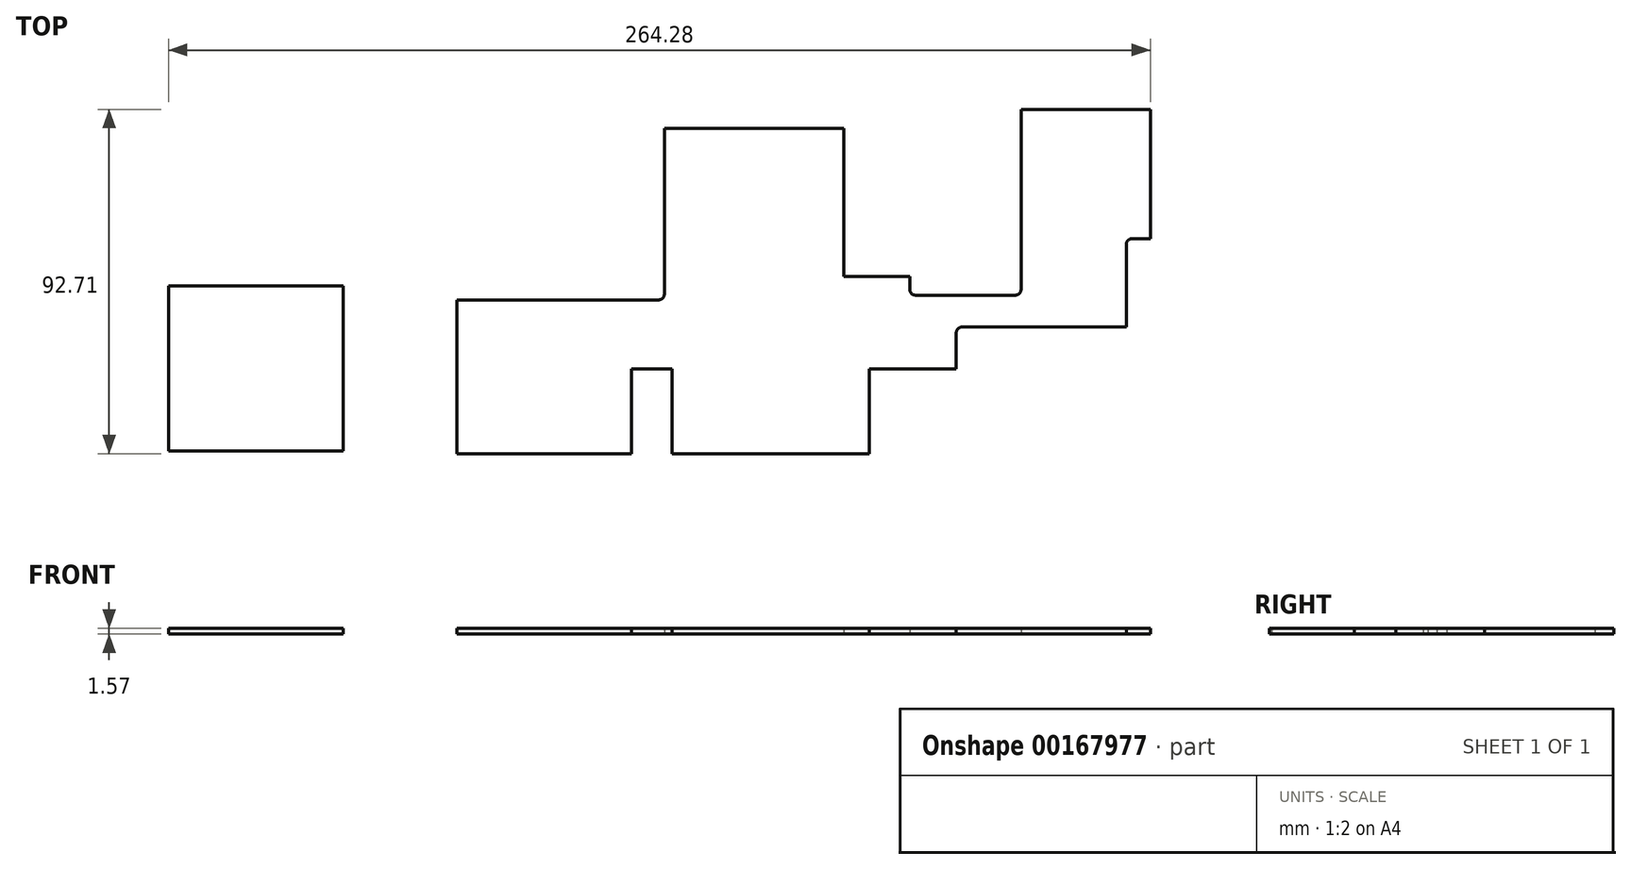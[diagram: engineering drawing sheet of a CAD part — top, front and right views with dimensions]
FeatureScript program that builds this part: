
annotation { "Feature Type Name" : "Feature", "Feature Type Description" : "" }
export const myFeature = defineFeature(function(context is Context, id is Id, definition is map)
    precondition{}
    {
        {
            var Q0;
            Q0=qCreatedBy(makeId("Top.planeOp"),FACE);
            var sketch = newSketch(context, id + "F0", { "sketchPlane" : qUnion([Q0])});
            skLineSegment(sketch, "E0.bottom", {"start": v(1.27, -0.7) * mm, "end": v(48.26, -0.7) * mm});
            skLineSegment(sketch, "E0.top", {"start": v(1.27, 40.7) * mm, "end": v(55.56, 40.7) * mm});
            skLineSegment(sketch, "E0.right", {"start": v(187.96, -0.7) * mm, "end": v(187.96, 22.66) * mm});
            skLineSegment(sketch, "E1.top", {"start": v(105.4, 86.92) * mm, "end": v(57.23, 86.92) * mm});
            skLineSegment(sketch, "E1.left", {"start": v(105.4, 53.4) * mm, "end": v(105.4, 86.92) * mm});
            skLineSegment(sketch, "E2.bottom", {"start": v(57.15, 45.77) * mm, "end": v(66.23, 45.77) * mm, "construction": true});
            skLineSegment(sketch, "E3", {"start": v(67.82, 47.36) * mm, "end": v(67.82, 86.92) * mm, "construction": true});
            skLineSegment(sketch, "E4", {"start": v(124.78, 41.96) * mm, "end": v(151.57, 41.96) * mm});
            skLineSegment(sketch, "E5.bottom", {"start": v(187.96, -0.7) * mm, "end": v(173.99, -0.7) * mm});
            skLineSegment(sketch, "E5.top", {"start": v(187.96, 92) * mm, "end": v(153.16, 92) * mm});
            skLineSegment(sketch, "E5.left", {"start": v(187.96, -0.7) * mm, "end": v(187.96, 22.66) * mm, "construction": true});
            skLineSegment(sketch, "E6.bottom", {"start": v(187.96, -0.7) * mm, "end": v(153.16, -0.7) * mm});
            skLineSegment(sketch, "E6.top", {"start": v(172.4, 74.22) * mm, "end": v(153.16, 74.22) * mm});
            skLineSegment(sketch, "E6.right", {"start": v(153.16, 43.55) * mm, "end": v(153.16, 74.22) * mm});
            skLineSegment(sketch, "E7.trimOffspring", {"start": v(173.99, 75.8) * mm, "end": v(173.99, 92) * mm});
            skLineSegment(sketch, "E8.bottom", {"start": v(187.96, 22.66) * mm, "end": v(183.07, 22.66) * mm});
            skLineSegment(sketch, "E8.top", {"start": v(187.96, 57.2) * mm, "end": v(183.07, 57.2) * mm});
            skLineSegment(sketch, "E8.right", {"start": v(181.48, 24.25) * mm, "end": v(181.48, 55.62) * mm});
            skLineSegment(sketch, "E9.trimOffspring", {"start": v(187.96, 57.2) * mm, "end": v(187.96, 92) * mm});
            skLineSegment(sketch, "E10.trimOffspring", {"start": v(187.96, 57.2) * mm, "end": v(187.96, 74.22) * mm});
            skLineSegment(sketch, "E11.bottom", {"start": v(105.4, 47.04) * mm, "end": v(123.2, 47.04) * mm});
            skLineSegment(sketch, "E11.top", {"start": v(123.2, -0.7) * mm, "end": v(123.19, -0.7) * mm});
            skLineSegment(sketch, "E11.right", {"start": v(123.2, 47.04) * mm, "end": v(123.2, 43.55) * mm});
            skLineSegment(sketch, "E12.bottom", {"start": v(105.4, 47.04) * mm, "end": v(87.19, 47.04) * mm});
            skLineSegment(sketch, "E12.top", {"start": v(105.4, 53.4) * mm, "end": v(87.19, 53.4) * mm});
            skLineSegment(sketch, "E12.right", {"start": v(85.6, 48.63) * mm, "end": v(85.6, 51.8) * mm});
            skPoint(sketch, "E13.visualSharp", {"position": v(57.15, 40.7) * mm});
            skArc(sketch, "E13.filletArc", {"start": v(55.56, 40.7) * mm, "mid": v(56.69, 41.16) * mm, "end": v(57.15, 42.28) * mm});
            skPoint(sketch, "E14.visualSharp", {"position": v(67.82, 45.77) * mm});
            skArc(sketch, "E14.filletArc", {"start": v(66.23, 45.77) * mm, "mid": v(67.35, 46.24) * mm, "end": v(67.82, 47.36) * mm});
            skPoint(sketch, "E15.visualSharp", {"position": v(85.6, 53.4) * mm});
            skArc(sketch, "E15.filletArc", {"start": v(87.19, 53.4) * mm, "mid": v(86.06, 52.93) * mm, "end": v(85.6, 51.8) * mm});
            skPoint(sketch, "E16.visualSharp", {"position": v(85.6, 47.04) * mm});
            skArc(sketch, "E16.filletArc", {"start": v(85.6, 48.63) * mm, "mid": v(86.06, 47.5) * mm, "end": v(87.19, 47.04) * mm});
            skArc(sketch, "E17.filletArc", {"start": v(123.2, 43.55) * mm, "mid": v(123.65, 42.43) * mm, "end": v(124.78, 41.96) * mm});
            skPoint(sketch, "E18.visualSharp", {"position": v(153.16, 41.96) * mm});
            skArc(sketch, "E18.filletArc", {"start": v(151.57, 41.96) * mm, "mid": v(152.7, 42.43) * mm, "end": v(153.16, 43.55) * mm});
            skPoint(sketch, "E19.visualSharp", {"position": v(173.99, 74.22) * mm});
            skArc(sketch, "E19.filletArc", {"start": v(172.4, 74.22) * mm, "mid": v(173.53, 74.69) * mm, "end": v(173.99, 75.8) * mm});
            skPoint(sketch, "E20.visualSharp", {"position": v(181.48, 57.2) * mm});
            skArc(sketch, "E20.filletArc", {"start": v(183.07, 57.2) * mm, "mid": v(181.95, 56.74) * mm, "end": v(181.48, 55.62) * mm});
            skPoint(sketch, "E21.visualSharp", {"position": v(181.48, 22.66) * mm});
            skArc(sketch, "E21.filletArc", {"start": v(181.48, 24.25) * mm, "mid": v(181.95, 23.12) * mm, "end": v(183.07, 22.66) * mm});
            skLineSegment(sketch, "E22", {"start": v(1.27, 40.7) * mm, "end": v(1.27, -0.7) * mm});
            skPoint(sketch, "E23", {"position": v(15.7, 37.7) * mm});
            skPoint(sketch, "E24", {"position": v(55.78, 37.7) * mm});
            skCircle(sketch, "E25", {"center": v(5.65, 4.18) * mm, "radius": 1.59 * mm});
            skCircle(sketch, "E26", {"center": v(24.7, 4.18) * mm, "radius": 1.59 * mm});
            skCircle(sketch, "E27", {"center": v(43.75, 4.18) * mm, "radius": 1.59 * mm});
            skPoint(sketch, "E28", {"position": v(26.29, 4.18) * mm});
            skPoint(sketch, "E29", {"position": v(42.16, 4.18) * mm});
            skPoint(sketch, "E30", {"position": v(7.24, 4.18) * mm});
            skPoint(sketch, "E31", {"position": v(4.06, 4.18) * mm});
            skLineSegment(sketch, "E32.bottom", {"start": v(187.96, 92) * mm, "end": v(183.59, 92) * mm});
            skLineSegment(sketch, "E32.top", {"start": v(187.96, 87.37) * mm, "end": v(183.59, 87.37) * mm, "construction": true});
            skLineSegment(sketch, "E32.left", {"start": v(187.96, 92) * mm, "end": v(187.96, 87.37) * mm});
            skLineSegment(sketch, "E32.right", {"start": v(183.59, 92) * mm, "end": v(183.59, 87.37) * mm, "construction": true});
            skCircle(sketch, "E33", {"center": v(183.59, 87.37) * mm, "radius": 1.59 * mm});
            skLineSegment(sketch, "E34", {"start": v(183.59, 87.37) * mm, "end": v(183.59, 61.97) * mm, "construction": true});
            skCircle(sketch, "E35", {"center": v(183.59, 61.97) * mm, "radius": 1.59 * mm});
            skLineSegment(sketch, "E36.top", {"start": v(48.26, 22.15) * mm, "end": v(59.18, 22.15) * mm});
            skLineSegment(sketch, "E36.left", {"start": v(48.26, -0.7) * mm, "end": v(48.26, 22.15) * mm});
            skLineSegment(sketch, "E36.right", {"start": v(123.2, -0.7) * mm, "end": v(123.2, 22.15) * mm, "construction": true});
            skLineSegment(sketch, "E37.trimOffspring", {"start": v(58.37, -0.7) * mm, "end": v(112.27, -0.7) * mm});
            skLineSegment(sketch, "E38", {"start": v(153.16, 74.22) * mm, "end": v(153.16, 92) * mm});
            skLineSegment(sketch, "E39", {"start": v(57.15, 42.28) * mm, "end": v(57.23, 86.92) * mm});
            skLineSegment(sketch, "E40", {"start": v(85.6, 53.4) * mm, "end": v(57.17, 53.4) * mm});
            skLineSegment(sketch, "E41", {"start": v(105.4, 53.4) * mm, "end": v(105.4, 47.04) * mm});
            skLineSegment(sketch, "E42.bottom", {"start": v(123.2, 22.15) * mm, "end": v(112.27, 22.15) * mm});
            skLineSegment(sketch, "E43", {"start": v(59.18, 22.15) * mm, "end": v(59.18, -0.7) * mm});
            skLineSegment(sketch, "E44", {"start": v(112.27, 22.15) * mm, "end": v(112.27, -0.7) * mm});
            skLineSegment(sketch, "E45.trimOffspring", {"start": v(123.2, -0.7) * mm, "end": v(187.96, -0.7) * mm, "construction": true});
            skPoint(sketch, "E46.end.orphan", {"position": v(59.18, 0) * mm});
            skPoint(sketch, "E46.start.orphan", {"position": v(112.27, 0) * mm});
            skLineSegment(sketch, "E47", {"start": v(123.2, 22.15) * mm, "end": v(135.71, 22.15) * mm});
            skLineSegment(sketch, "E48", {"start": v(135.71, 22.15) * mm, "end": v(135.71, 31.8) * mm});
            skLineSegment(sketch, "E49", {"start": v(137.31, 33.4) * mm, "end": v(181.48, 33.4) * mm});
            skPoint(sketch, "E50.visualSharp", {"position": v(135.71, 33.4) * mm});
            skArc(sketch, "E50.filletArc", {"start": v(137.31, 33.4) * mm, "mid": v(136.18, 32.93) * mm, "end": v(135.71, 31.8) * mm});
            skSolve(sketch);
        }
        {
            var Q0;
            Q0=qCreatedBy(makeId("Top.planeOp"),FACE);
            var sketch = newSketch(context, id + "F1", { "sketchPlane" : qUnion([Q0])});
            skLineSegment(sketch, "E51.top", {"start": v(-76.32, 0) * mm, "end": v(-29.33, 0) * mm});
            skLineSegment(sketch, "E51.left", {"start": v(-76.32, 19.05) * mm, "end": v(-76.32, 0) * mm});
            skLineSegment(sketch, "E51.right", {"start": v(-29.33, 19.05) * mm, "end": v(-29.33, 0) * mm});
            skLineSegment(sketch, "E52.bottom", {"start": v(-29.33, 0) * mm, "end": v(-40.76, 0) * mm});
            skLineSegment(sketch, "E52.top", {"start": v(-29.33, 44.45) * mm, "end": v(-40.76, 44.45) * mm});
            skLineSegment(sketch, "E52.left", {"start": v(-29.33, 0) * mm, "end": v(-29.33, 44.45) * mm});
            skLineSegment(sketch, "E53.top", {"start": v(-76.32, 44.45) * mm, "end": v(-68.5, 44.45) * mm});
            skLineSegment(sketch, "E53.left", {"start": v(-76.32, 19.05) * mm, "end": v(-76.32, 44.45) * mm});
            skLineSegment(sketch, "E54", {"start": v(-68.5, 44.45) * mm, "end": v(-40.76, 44.45) * mm});
            skSolve(sketch);
        }
        {
            var Q0;
            Q0=makeQuery(id+"F0.imprint","IMPRINT",FACE,{"disambiguationData":[TD([[makeQuery(id+"F0.imprint","IMPRINT",EDGE,{"derivedFrom":sQuery(id+"F0.wireOp",EDGE,"E12.bottom")}),-1.0]])]});
            var Q1;
            Q1=makeQuery(id+"F0.imprint","IMPRINT",FACE,{"disambiguationData":[TD([[makeQuery(id+"F0.imprint","IMPRINT",EDGE,{"derivedFrom":sQuery(id+"F0.wireOp",EDGE,"E0.bottom")}),1.0]])]});
            var Q2;
            Q2=makeQuery(id+"F0.imprint","IMPRINT",FACE,{"disambiguationData":[TD([[makeQuery(id+"F0.imprint","IMPRINT",EDGE,{"derivedFrom":sQuery(id+"F0.wireOp",EDGE,"E6.top")}),-1.0]])]});
            var Q3;
            Q3=makeQuery(id+"F1.imprint","IMPRINT",FACE,{"disambiguationData":[TD([[makeQuery(id+"F1.imprint","IMPRINT",EDGE,{"derivedFrom":sQuery(id+"F1.wireOp",EDGE,"E51.top")}),1.0]])]});
            var Q4;
            Q4=makeQuery(id+"F0.imprint","IMPRINT",FACE,{"disambiguationData":[TD([[makeQuery(id+"F0.imprint","IMPRINT",EDGE,{"derivedFrom":sQuery(id+"F0.wireOp",EDGE,"E33")}),1.0]])]});
            var Q5;
            Q5=makeQuery(id+"F0.imprint","IMPRINT",FACE,{"disambiguationData":[TD([[makeQuery(id+"F0.imprint","IMPRINT",EDGE,{"derivedFrom":sQuery(id+"F0.wireOp",EDGE,"E27")}),1.0]])]});
            var Q6;
            Q6=makeQuery(id+"F0.imprint","IMPRINT",FACE,{"disambiguationData":[TD([[makeQuery(id+"F0.imprint","IMPRINT",EDGE,{"derivedFrom":sQuery(id+"F0.wireOp",EDGE,"E26")}),1.0]])]});
            var Q7;
            Q7=makeQuery(id+"F0.imprint","IMPRINT",FACE,{"disambiguationData":[TD([[makeQuery(id+"F0.imprint","IMPRINT",EDGE,{"derivedFrom":sQuery(id+"F0.wireOp",EDGE,"E25")}),1.0]])]});
            var Q8;
            Q8=makeQuery(id+"F0.imprint","IMPRINT",FACE,{"disambiguationData":[TD([[makeQuery(id+"F0.imprint","IMPRINT",EDGE,{"derivedFrom":sQuery(id+"F0.wireOp",EDGE,"E35")}),1.0]])]});
            extrude(context, id + "F2", {"entities" : qUnion([Q0, Q1, Q2, Q3, Q4, Q5, Q6, Q7, Q8]), "depth" : 1.57 * mm, "offsetDistance" : 25.4 * mm});
        }
    });
